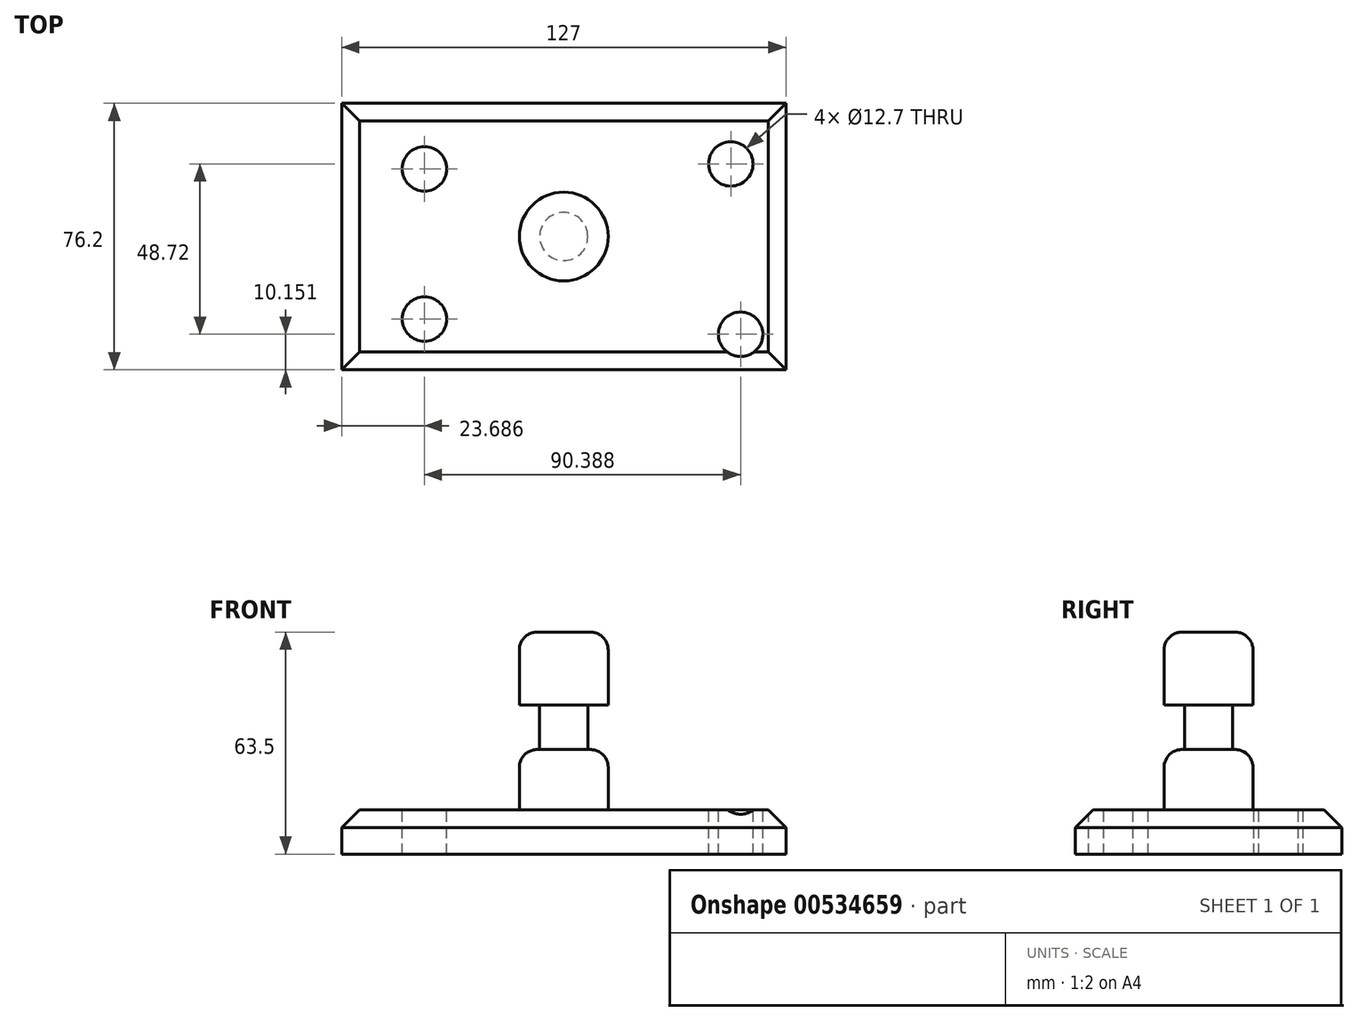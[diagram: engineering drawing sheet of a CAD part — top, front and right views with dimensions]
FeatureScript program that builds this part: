
annotation { "Feature Type Name" : "Feature", "Feature Type Description" : "" }
export const myFeature = defineFeature(function(context is Context, id is Id, definition is map)
    precondition{}
    {
        {
            var Q0;
            Q0=qCreatedBy(makeId("Top.planeOp"),FACE);
            var sketch = newSketch(context, id + "F0", { "sketchPlane" : qUnion([Q0])});
            skLineSegment(sketch, "E0.bottom", {"start": v(63.5, 38.1) * mm, "end": v(-63.5, 38.1) * mm});
            skLineSegment(sketch, "E0.top", {"start": v(63.5, -38.1) * mm, "end": v(-63.5, -38.1) * mm});
            skLineSegment(sketch, "E0.left", {"start": v(63.5, 38.1) * mm, "end": v(63.5, -38.1) * mm});
            skLineSegment(sketch, "E0.right", {"start": v(-63.5, 38.1) * mm, "end": v(-63.5, -38.1) * mm});
            skPoint(sketch, "E0.middle", {"position": v(0, 0) * mm});
            skSolve(sketch);
        }
        {
            var Q0;
            Q0=makeQuery(id+"F0.imprint","IMPRINT",FACE,{"disambiguationData":[TD([[makeQuery(id+"F0.imprint","IMPRINT",EDGE,{"derivedFrom":sQuery(id+"F0.wireOp",EDGE,"E0.bottom")}),1.0]])]});
            extrude(context, id + "F1", {"entities" : qUnion([Q0]), "depth" : 12.7 * mm, "offsetDistance" : 25.4 * mm});
        }
        {
            var Q0;
            Q0=makeQuery(id+"F1.opExtrude","CAP_FACE",FACE,{"disambiguationData":[OSD([sQuery(id+"F0.wireOp",EDGE,"E0.bottom"),sQuery(id+"F0.wireOp",EDGE,"E0.top"),sQuery(id+"F0.wireOp",EDGE,"E0.left"),sQuery(id+"F0.wireOp",EDGE,"E0.right")])],"isStart":false});
            var sketch = newSketch(context, id + "F2", { "sketchPlane" : qUnion([Q0])});
            skCircle(sketch, "E1", {"center": v(50.57, -27.95) * mm, "radius": 6.35 * mm});
            skCircle(sketch, "E2", {"center": v(47.75, 20.77) * mm, "radius": 6.35 * mm});
            skCircle(sketch, "E3", {"center": v(-39.81, -23.59) * mm, "radius": 6.35 * mm});
            skCircle(sketch, "E4", {"center": v(-39.81, 19.35) * mm, "radius": 6.35 * mm});
            skSolve(sketch);
        }
        {
            var Q0;
            Q0=makeQuery(id+"F2.imprint","IMPRINT",FACE,{"disambiguationData":[TD([[makeQuery(id+"F2.imprint","IMPRINT",EDGE,{"derivedFrom":sQuery(id+"F2.wireOp",EDGE,"E3")}),1.0]])]});
            var Q1;
            Q1=makeQuery(id+"F2.imprint","IMPRINT",FACE,{"disambiguationData":[TD([[makeQuery(id+"F2.imprint","IMPRINT",EDGE,{"derivedFrom":sQuery(id+"F2.wireOp",EDGE,"E2")}),1.0]])]});
            var Q2;
            Q2=makeQuery(id+"F2.imprint","IMPRINT",FACE,{"disambiguationData":[TD([[makeQuery(id+"F2.imprint","IMPRINT",EDGE,{"derivedFrom":sQuery(id+"F2.wireOp",EDGE,"E4")}),1.0]])]});
            var Q3;
            Q3=makeQuery(id+"F2.imprint","IMPRINT",FACE,{"disambiguationData":[TD([[makeQuery(id+"F2.imprint","IMPRINT",EDGE,{"derivedFrom":sQuery(id+"F2.wireOp",EDGE,"E1")}),1.0]])]});
            extrude(context, id + "F3", {"entities" : qUnion([Q0, Q1, Q2, Q3]), "operationType" : NewBodyOperationType.REMOVE, "endBound" : BoundingType.THROUGH_ALL, "oppositeDirection" : true, "depth" : 38.1 * mm, "offsetDistance" : 25.4 * mm});
        }
        {
            var Q0;
            Q0=qCreatedBy(makeId("Front.planeOp"),FACE);
            var sketch = newSketch(context, id + "F4", { "sketchPlane" : qUnion([Q0])});
            skLineSegment(sketch, "E5.bottom", {"start": v(0, 12.7) * mm, "end": v(12.7, 12.7) * mm});
            skLineSegment(sketch, "E5.top", {"start": v(0, 63.5) * mm, "end": v(12.7, 63.5) * mm});
            skLineSegment(sketch, "E5.left", {"start": v(0, 12.7) * mm, "end": v(0, 63.5) * mm});
            skLineSegment(sketch, "E5.right", {"start": v(12.7, 12.7) * mm, "end": v(12.7, 63.5) * mm});
            skSolve(sketch);
        }
        {
            var Q0;
            Q0=makeQuery(id+"F4.imprint","IMPRINT",FACE,{"disambiguationData":[TD([[makeQuery(id+"F4.imprint","IMPRINT",EDGE,{"derivedFrom":sQuery(id+"F4.wireOp",EDGE,"E5.bottom")}),1.0]])]});
            var Q1;
            Q1=sQuery(id+"F4.wireOp",EDGE,"E5.left");
            revolve(context, id + "F5", {"operationType" : NewBodyOperationType.ADD, "entities" : qUnion([Q0]), "axis" : qUnion([Q1]), "revolveType" : RevolveType.FULL});
        }
        {
            var Q0;
            Q0=qCreatedBy(makeId("Front.planeOp"),FACE);
            var sketch = newSketch(context, id + "F6", { "sketchPlane" : qUnion([Q0])});
            skLineSegment(sketch, "E6.bottom", {"start": v(6.89, 42.61) * mm, "end": v(14.5, 42.61) * mm});
            skLineSegment(sketch, "E6.top", {"start": v(6.89, 29.91) * mm, "end": v(14.5, 29.91) * mm});
            skLineSegment(sketch, "E6.left", {"start": v(6.89, 42.61) * mm, "end": v(6.89, 29.91) * mm});
            skLineSegment(sketch, "E6.right", {"start": v(14.5, 42.61) * mm, "end": v(14.5, 29.91) * mm});
            skSolve(sketch);
        }
        {
            var Q0;
            Q0=makeQuery(id+"F6.imprint","IMPRINT",FACE,{"disambiguationData":[TD([[makeQuery(id+"F6.imprint","IMPRINT",EDGE,{"derivedFrom":sQuery(id+"F6.wireOp",EDGE,"E6.bottom")}),-1.0]])]});
            var Q1;
            Q1=makeQuery(id+"F5.opRevolve","SWEPT_FACE",FACE,{"disambiguationData":[OSD([sQuery(id+"F4.wireOp",EDGE,"E5.right")])]});
            revolve(context, id + "F7", {"operationType" : NewBodyOperationType.REMOVE, "entities" : qUnion([Q0]), "axis" : qUnion([Q1]), "revolveType" : RevolveType.FULL, "oppositeDirection" : true});
        }
        {
            var Q0;
            Q0=makeQuery(id+"F7.boolean.opBoolean","INTERSECT",EDGE,{"derivedFrom":[makeQuery(id+"F5.opRevolve","SWEPT_FACE",FACE,{"disambiguationData":[OSD([sQuery(id+"F4.wireOp",EDGE,"E5.right")])]}),makeQuery(id+"F7.opRevolve","SWEPT_FACE",FACE,{"disambiguationData":[OSD([sQuery(id+"F6.wireOp",EDGE,"E6.top")])]})]});
            var Q1;
            Q1=makeQuery(id+"F5.opRevolve","SWEPT_EDGE",EDGE,{"disambiguationData":[OSD([sQuery(id+"F4.wireOp",EDGE,"E5.top"),sQuery(id+"F4.wireOp",EDGE,"E5.right")])]});
            var Q2;
            Q2=makeQuery(id+"F5.opRevolve","SWEPT_EDGE",EDGE,{"disambiguationData":[OSD([sQuery(id+"F4.wireOp",EDGE,"E5.bottom"),sQuery(id+"F4.wireOp",EDGE,"E5.right")])]});
            fillet(context, id + "F8", {"entities" : qUnion([Q0, Q1, Q2]), "radius" : 5.08 * mm, "tangentPropagation" : true, "allowEdgeOverflow" : false});
        }
        {
            var Q0;
            Q0=makeQuery(id+"F8.opFillet","BLEND_FACE",FACE,{"disambiguationData":[OSD([sQuery(id+"F4.wireOp",EDGE,"E5.right"),sQuery(id+"F6.wireOp",EDGE,"E6.top")])]});
            var Q1;
            Q1=makeQuery(id+"F1.opExtrude","CAP_EDGE",EDGE,{"disambiguationData":[OSD([sQuery(id+"F0.wireOp",EDGE,"E0.bottom")])],"isStart":false});
            var Q2;
            Q2=makeQuery(id+"F1.opExtrude","CAP_EDGE",EDGE,{"disambiguationData":[OSD([sQuery(id+"F0.wireOp",EDGE,"E0.left")])],"isStart":false});
            var Q3;
            Q3=makeQuery(id+"F1.opExtrude","CAP_EDGE",EDGE,{"disambiguationData":[OSD([sQuery(id+"F0.wireOp",EDGE,"E0.top")])],"isStart":false});
            var Q4;
            Q4=makeQuery(id+"F1.opExtrude","CAP_EDGE",EDGE,{"disambiguationData":[OSD([sQuery(id+"F0.wireOp",EDGE,"E0.right")])],"isStart":false});
            chamfer(context, id + "F9", {"entities" : qUnion([Q0, Q1, Q2, Q3, Q4]), "width" : 5.08 * mm, "tangentPropagation" : true});
        }
    });
